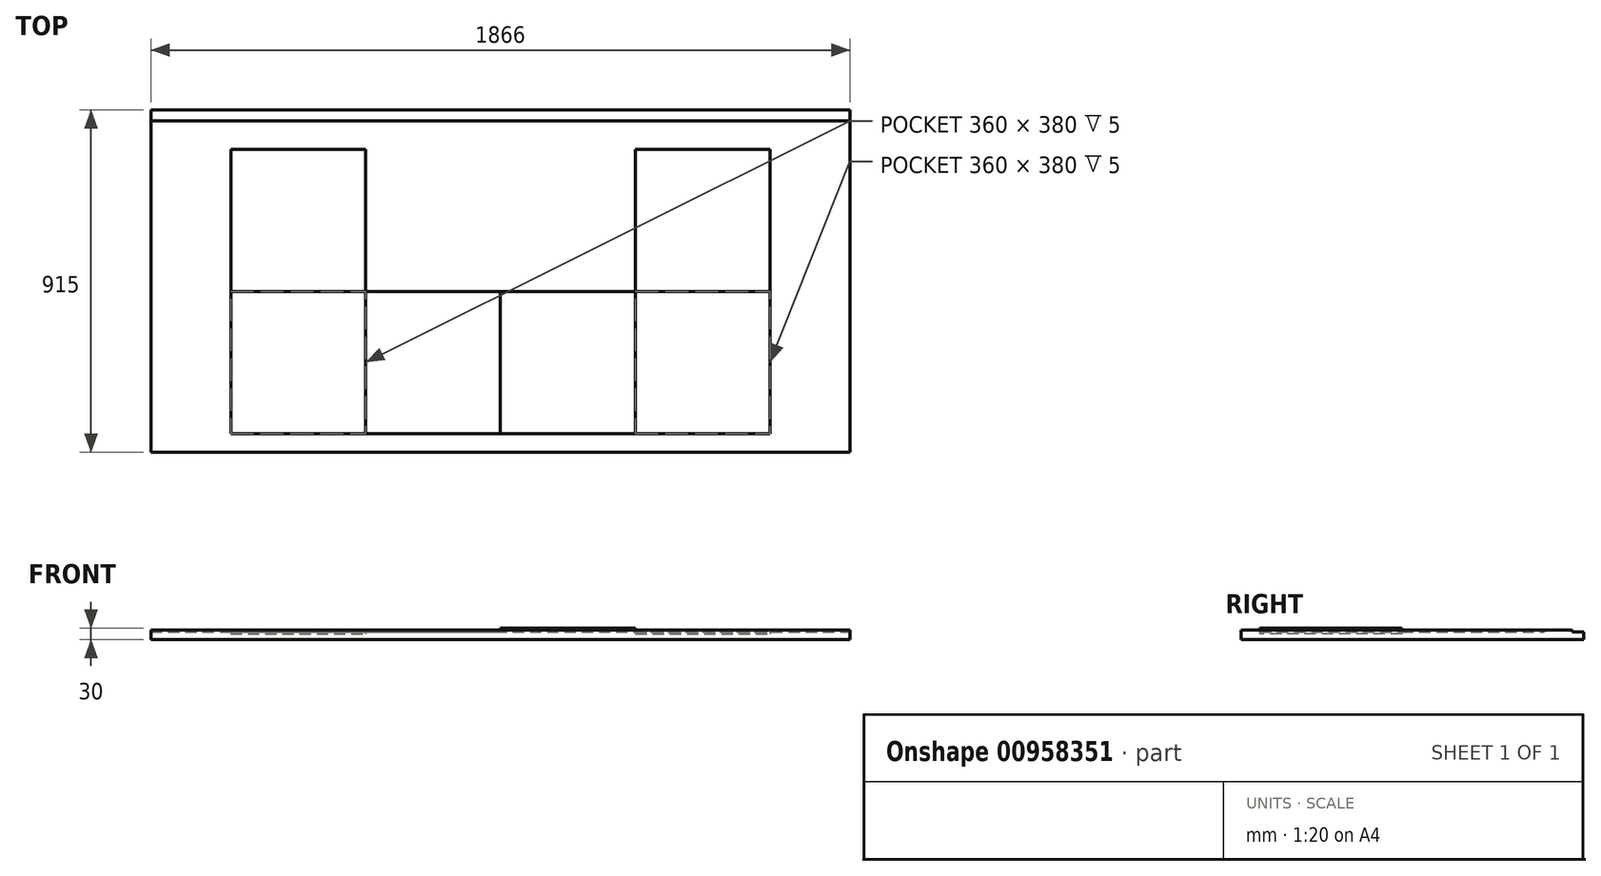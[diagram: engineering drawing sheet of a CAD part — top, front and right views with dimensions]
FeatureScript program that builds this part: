
annotation { "Feature Type Name" : "Feature", "Feature Type Description" : "" }
export const myFeature = defineFeature(function(context is Context, id is Id, definition is map)
    precondition{}
    {
        {
            var Q0;
            Q0=qCreatedBy(makeId("Top.planeOp"),FACE);
            var sketch = newSketch(context, id + "F0", { "sketchPlane" : qUnion([Q0])});
            skLineSegment(sketch, "E0.bottom", {"start": v(0, 0) * mm, "end": v(1866, 0) * mm});
            skLineSegment(sketch, "E0.top", {"start": v(0, 915) * mm, "end": v(1866, 915) * mm});
            skLineSegment(sketch, "E0.left", {"start": v(0, 0) * mm, "end": v(0, 915) * mm});
            skLineSegment(sketch, "E0.right", {"start": v(1866, 0) * mm, "end": v(1866, 915) * mm});
            skLineSegment(sketch, "E1", {"start": v(0, 885) * mm, "end": v(1866, 885) * mm});
            skLineSegment(sketch, "E2.bottom", {"start": v(213, 50) * mm, "end": v(573, 50) * mm});
            skLineSegment(sketch, "E2.top", {"start": v(213, 430) * mm, "end": v(573, 430) * mm});
            skLineSegment(sketch, "E2.left", {"start": v(213, 50) * mm, "end": v(213, 430) * mm});
            skLineSegment(sketch, "E2.right", {"start": v(573, 50) * mm, "end": v(573, 430) * mm});
            skLineSegment(sketch, "E3.top", {"start": v(213, 810) * mm, "end": v(573, 810) * mm});
            skLineSegment(sketch, "E3.left", {"start": v(213, 430) * mm, "end": v(213, 810) * mm});
            skLineSegment(sketch, "E3.right", {"start": v(573, 430) * mm, "end": v(573, 810) * mm});
            skLineSegment(sketch, "E4.bottom", {"start": v(573, 430) * mm, "end": v(933, 430) * mm});
            skLineSegment(sketch, "E4.top", {"start": v(573, 50) * mm, "end": v(933, 50) * mm});
            skLineSegment(sketch, "E4.left", {"start": v(573, 430) * mm, "end": v(573, 50) * mm});
            skLineSegment(sketch, "E4.right", {"start": v(933, 430) * mm, "end": v(933, 50) * mm});
            skLineSegment(sketch, "E5.bottom", {"start": v(933, 430) * mm, "end": v(1293, 430) * mm});
            skLineSegment(sketch, "E5.top", {"start": v(933, 50) * mm, "end": v(1293, 50) * mm});
            skLineSegment(sketch, "E5.right", {"start": v(1293, 430) * mm, "end": v(1293, 50) * mm});
            skLineSegment(sketch, "E6.bottom", {"start": v(1293, 430) * mm, "end": v(1653, 430) * mm});
            skLineSegment(sketch, "E6.top", {"start": v(1293, 50) * mm, "end": v(1653, 50) * mm});
            skLineSegment(sketch, "E6.right", {"start": v(1653, 430) * mm, "end": v(1653, 50) * mm});
            skLineSegment(sketch, "E7.top", {"start": v(1293, 810) * mm, "end": v(1653, 810) * mm});
            skLineSegment(sketch, "E7.left", {"start": v(1293, 430) * mm, "end": v(1293, 810) * mm});
            skLineSegment(sketch, "E7.right", {"start": v(1653, 430) * mm, "end": v(1653, 810) * mm});
            skSolve(sketch);
        }
        {
            var Q0;
            {var subQ0=sQuery(id+"F0.wireOp",EDGE,"E0.bottom");Q0=makeQuery(id+"F0.imprint","IMPRINT",FACE,{"disambiguationData":[TD([[makeQuery(id+"F0.imprint","IMPRINT",EDGE,{"derivedFrom":subQ0}),1.0]])]});}
            extrude(context, id + "F1", {"entities" : qUnion([Q0]), "depth" : 25 * mm, "offsetDistance" : 25 * mm});
        }
        {
            var Q0;
            {var subQ0=sQuery(id+"F0.wireOp",EDGE,"E0.top");Q0=makeQuery(id+"F0.imprint","IMPRINT",FACE,{"disambiguationData":[TD([[makeQuery(id+"F0.imprint","IMPRINT",EDGE,{"derivedFrom":subQ0}),-1.0]])]});}
            var Q1;
            Q1=makeQuery(id+"F0.imprint","IMPRINT",FACE,{"disambiguationData":[TD([[makeQuery(id+"F0.imprint","IMPRINT",EDGE,{"derivedFrom":sQuery(id+"F0.wireOp",EDGE,"E2.top")}),1.0]])]});
            var Q2;
            Q2=makeQuery(id+"F0.imprint","IMPRINT",FACE,{"disambiguationData":[TD([[makeQuery(id+"F0.imprint","IMPRINT",EDGE,{"derivedFrom":sQuery(id+"F0.wireOp",EDGE,"E4.bottom")}),-1.0]])]});
            var Q3;
            Q3=makeQuery(id+"F0.imprint","IMPRINT",FACE,{"disambiguationData":[TD([[makeQuery(id+"F0.imprint","IMPRINT",EDGE,{"derivedFrom":sQuery(id+"F0.wireOp",EDGE,"E6.bottom")}),1.0]])]});
            extrude(context, id + "F2", {"entities" : qUnion([Q0, Q1, Q2, Q3]), "operationType" : NewBodyOperationType.ADD, "depth" : 20 * mm, "offsetDistance" : 25 * mm});
        }
        {
            var Q0;
            Q0=makeQuery(id+"F0.imprint","IMPRINT",FACE,{"disambiguationData":[TD([[makeQuery(id+"F0.imprint","IMPRINT",EDGE,{"derivedFrom":sQuery(id+"F0.wireOp",EDGE,"E6.top")}),1.0]])]});
            var Q1;
            Q1=makeQuery(id+"F0.imprint","IMPRINT",FACE,{"disambiguationData":[TD([[makeQuery(id+"F0.imprint","IMPRINT",EDGE,{"derivedFrom":sQuery(id+"F0.wireOp",EDGE,"E2.bottom")}),1.0]])]});
            extrude(context, id + "F3", {"entities" : qUnion([Q0, Q1]), "operationType" : NewBodyOperationType.ADD, "depth" : 15 * mm, "offsetDistance" : 25 * mm});
        }
        {
            var Q0;
            Q0=makeQuery(id+"F0.imprint","IMPRINT",FACE,{"disambiguationData":[TD([[makeQuery(id+"F0.imprint","IMPRINT",EDGE,{"derivedFrom":sQuery(id+"F0.wireOp",EDGE,"E5.bottom")}),-1.0]])]});
            extrude(context, id + "F4", {"entities" : qUnion([Q0]), "operationType" : NewBodyOperationType.ADD, "depth" : 30 * mm, "offsetDistance" : 25 * mm});
        }
    });
